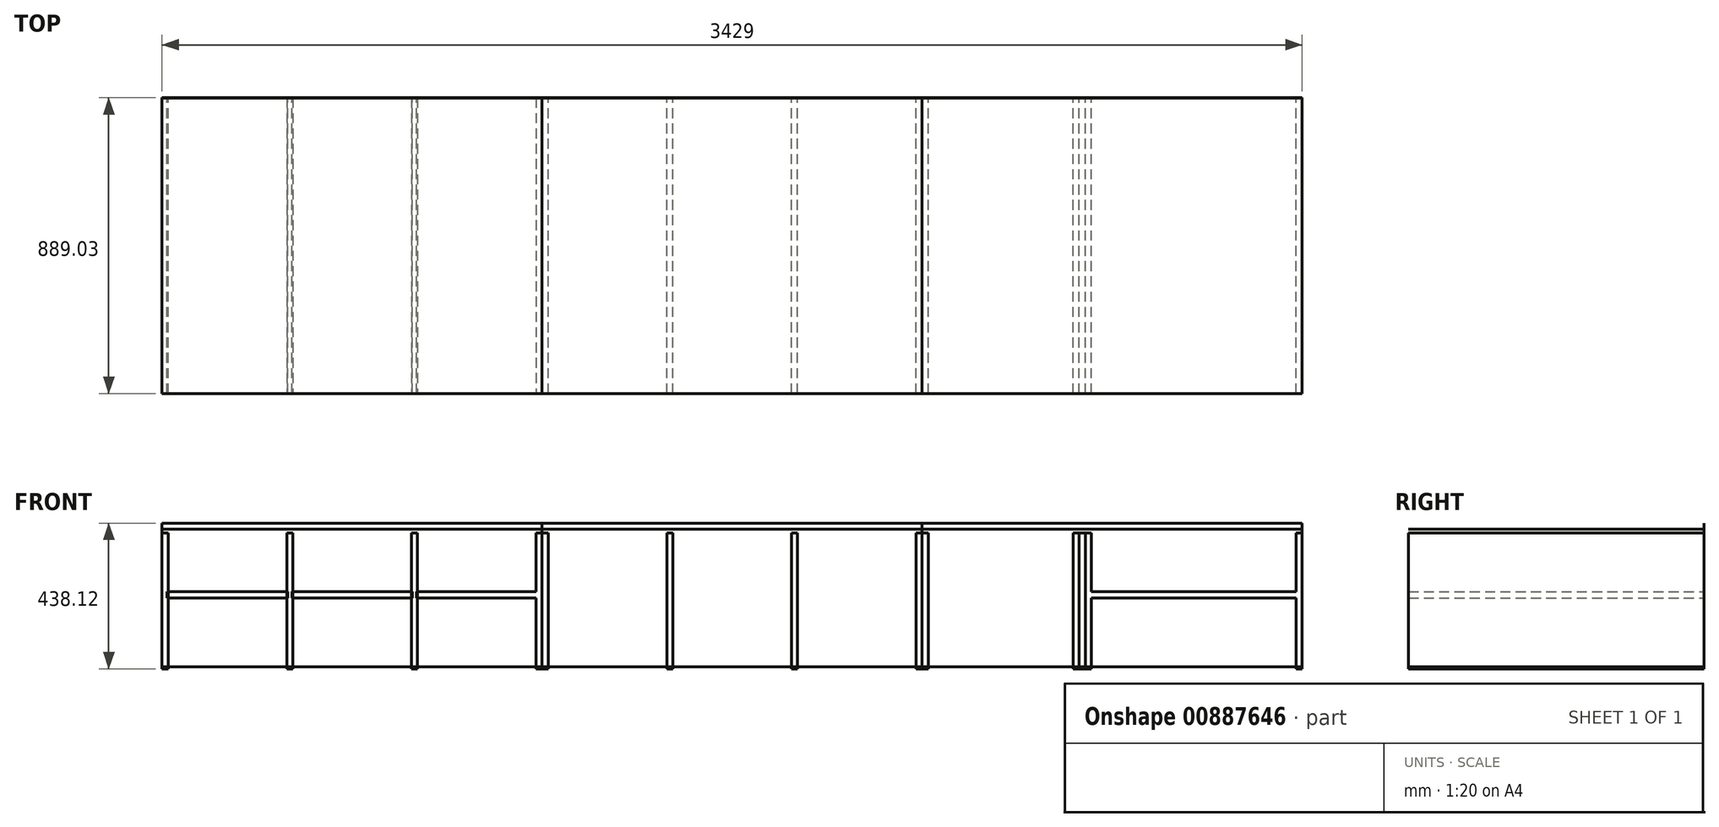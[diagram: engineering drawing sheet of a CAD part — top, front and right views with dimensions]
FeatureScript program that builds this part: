
annotation { "Feature Type Name" : "Feature", "Feature Type Description" : "" }
export const myFeature = defineFeature(function(context is Context, id is Id, definition is map)
    precondition{}
    {
        {
            var Q0;
            Q0=qCreatedBy(makeId("Front.planeOp"),FACE);
            var sketch = newSketch(context, id + "F0", { "sketchPlane" : qUnion([Q0])});
            skLineSegment(sketch, "E0.bottom", {"start": v(0, 0) * mm, "end": v(3429, 0) * mm, "construction": true});
            skLineSegment(sketch, "E0.top", {"start": v(0, 558.8) * mm, "end": v(3429, 558.8) * mm, "construction": true});
            skLineSegment(sketch, "E0.left", {"start": v(0, 0) * mm, "end": v(0, 558.8) * mm, "construction": true});
            skLineSegment(sketch, "E0.right", {"start": v(3429, 0) * mm, "end": v(3429, 558.8) * mm, "construction": true});
            skLineSegment(sketch, "E1", {"start": v(1714.5, 558.8) * mm, "end": v(1714.5, 0) * mm, "construction": true});
            skPoint(sketch, "E2", {"position": v(393.7, 558.8) * mm});
            skPoint(sketch, "E3", {"position": v(3035.3, 558.8) * mm});
            skSolve(sketch);
        }
        {
            var Q0;
            Q0=qCreatedBy(makeId("Top.planeOp"),FACE);
            var sketch = newSketch(context, id + "F1", { "sketchPlane" : qUnion([Q0])});
            skLineSegment(sketch, "E4.bottom", {"start": v(0, 0) * mm, "end": v(3429, 0) * mm, "construction": true});
            skLineSegment(sketch, "E4.top", {"start": v(0, -889) * mm, "end": v(3429, -889) * mm, "construction": true});
            skLineSegment(sketch, "E4.left", {"start": v(0, 0) * mm, "end": v(0, -889) * mm, "construction": true});
            skLineSegment(sketch, "E4.right", {"start": v(3429, 0) * mm, "end": v(3429, -889) * mm, "construction": true});
            skPoint(sketch, "E5.0", {"position": v(1714.5, 0) * mm});
            skLineSegment(sketch, "E6", {"start": v(1714.5, 0) * mm, "end": v(1714.5, -889) * mm, "construction": true});
            skPoint(sketch, "E7", {"position": v(3035.3, -889) * mm});
            skPoint(sketch, "E8", {"position": v(393.7, -889) * mm});
            skLineSegment(sketch, "E9", {"start": v(0, -444.5) * mm, "end": v(3429, -444.5) * mm, "construction": true});
            skPoint(sketch, "E10", {"position": v(0, -793.75) * mm});
            skPoint(sketch, "E11", {"position": v(0, -95.25) * mm});
            skPoint(sketch, "E12", {"position": v(3429, -95.25) * mm});
            skPoint(sketch, "E13", {"position": v(3429, -793.75) * mm});
            skPoint(sketch, "E14", {"position": v(1143, -889) * mm});
            skPoint(sketch, "E15", {"position": v(2286, -889) * mm});
            skSolve(sketch);
        }
        {
            var Q0;
            Q0=qCreatedBy(makeId("Top.planeOp"),FACE);
            var sketch = newSketch(context, id + "F2", { "sketchPlane" : qUnion([Q0])});
            skPoint(sketch, "E16.0", {"position": v(0, 0) * mm});
            skPoint(sketch, "E17.0", {"position": v(0, -889) * mm});
            skPoint(sketch, "E18.0", {"position": v(3429, -889) * mm});
            skPoint(sketch, "E19.0", {"position": v(3429, 0) * mm});
            skPoint(sketch, "E20.0", {"position": v(1143, -889) * mm});
            skPoint(sketch, "E21.0", {"position": v(2286, -889) * mm});
            skLineSegment(sketch, "E22.0", {"start": v(0, 0) * mm, "end": v(3429, 0) * mm, "construction": true});
            skLineSegment(sketch, "E23.bottom", {"start": v(0, 0) * mm, "end": v(1143, 0) * mm});
            skLineSegment(sketch, "E23.top", {"start": v(0, -889) * mm, "end": v(1143, -889) * mm});
            skLineSegment(sketch, "E23.left", {"start": v(0, 0) * mm, "end": v(0, -889) * mm});
            skLineSegment(sketch, "E23.right", {"start": v(1143, 0) * mm, "end": v(1143, -889) * mm});
            skLineSegment(sketch, "E24.bottom", {"start": v(1143, -889) * mm, "end": v(2286, -889) * mm});
            skLineSegment(sketch, "E24.top", {"start": v(1143, 0) * mm, "end": v(2286, 0) * mm});
            skLineSegment(sketch, "E24.left", {"start": v(1143, -889) * mm, "end": v(1143, 0) * mm});
            skLineSegment(sketch, "E24.right", {"start": v(2286, -889) * mm, "end": v(2286, 0) * mm});
            skLineSegment(sketch, "E25.bottom", {"start": v(2286, 0) * mm, "end": v(3429, 0) * mm});
            skLineSegment(sketch, "E25.top", {"start": v(2286, -889) * mm, "end": v(3429, -889) * mm});
            skLineSegment(sketch, "E25.left", {"start": v(2286, 0) * mm, "end": v(2286, -889) * mm});
            skLineSegment(sketch, "E25.right", {"start": v(3429, 0) * mm, "end": v(3429, -889) * mm});
            skSolve(sketch);
        }
        {
            var Q0;
            Q0=makeQuery(id+"F2.imprint","IMPRINT",FACE,{"disambiguationData":[TD([[makeQuery(id+"F2.imprint","IMPRINT",EDGE,{"derivedFrom":sQuery(id+"F2.wireOp",EDGE,"E23.bottom")}),-1.0]])]});
            extrude(context, id + "F3", {"entities" : qUnion([Q0]), "depth" : 23 / 812.8 * mm, "offsetDistance" : 25.4 * mm});
        }
        {
            var Q0;
            Q0=makeQuery(id+"F2.imprint","IMPRINT",FACE,{"disambiguationData":[TD([[makeQuery(id+"F2.imprint","IMPRINT",EDGE,{"derivedFrom":sQuery(id+"F2.wireOp",EDGE,"E24.bottom")}),1.0]])]});
            extrude(context, id + "F4", {"entities" : qUnion([Q0]), "depth" : 23 / 812.8 * mm, "offsetDistance" : 25.4 * mm});
        }
        {
            var Q0;
            Q0=makeQuery(id+"F2.imprint","IMPRINT",FACE,{"disambiguationData":[TD([[makeQuery(id+"F2.imprint","IMPRINT",EDGE,{"derivedFrom":sQuery(id+"F2.wireOp",EDGE,"E25.bottom")}),-1.0]])]});
            extrude(context, id + "F5", {"entities" : qUnion([Q0]), "depth" : 23 / 812.8 * mm, "offsetDistance" : 25.4 * mm});
        }
        {
            var Q0;
            Q0=makeQuery(id+"F3.opExtrude","CAP_FACE",FACE,{"disambiguationData":[OSD([sQuery(id+"F2.wireOp",EDGE,"E23.bottom"),sQuery(id+"F2.wireOp",EDGE,"E23.top"),sQuery(id+"F2.wireOp",EDGE,"E23.left"),sQuery(id+"F2.wireOp",EDGE,"E24.left")])],"isStart":false});
            var sketch = newSketch(context, id + "F6", { "sketchPlane" : qUnion([Q0])});
            skLineSegment(sketch, "E26.bottom", {"start": v(1143, -889) * mm, "end": v(1124.74, -889) * mm});
            skLineSegment(sketch, "E26.top", {"start": v(1143, 0) * mm, "end": v(1124.74, 0) * mm});
            skLineSegment(sketch, "E26.left", {"start": v(1143, -889) * mm, "end": v(1143, 0) * mm});
            skLineSegment(sketch, "E26.right", {"start": v(1124.74, -889) * mm, "end": v(1124.74, 0) * mm});
            skSolve(sketch);
        }
        {
            var Q0;
            Q0=makeQuery(id+"F6.imprint","IMPRINT",FACE,{"disambiguationData":[TD([[makeQuery(id+"F6.imprint","IMPRINT",EDGE,{"derivedFrom":sQuery(id+"F6.wireOp",EDGE,"E26.bottom")}),1.0]])]});
            extrude(context, id + "F7", {"entities" : qUnion([Q0]), "depth" : 401.64 * mm, "offsetDistance" : 25.4 * mm, "hasSecondDirection" : true, "secondDirectionOppositeDirection" : true, "secondDirectionDepth" : 6.35 * mm});
        }
        {
            var Q0;
            Q0=makeQuery(id+"F3.opExtrude","CAP_FACE",FACE,{"disambiguationData":[OSD([sQuery(id+"F2.wireOp",EDGE,"E23.bottom"),sQuery(id+"F2.wireOp",EDGE,"E23.top"),sQuery(id+"F2.wireOp",EDGE,"E23.left"),sQuery(id+"F2.wireOp",EDGE,"E24.left")])],"isStart":false});
            var sketch = newSketch(context, id + "F8", { "sketchPlane" : qUnion([Q0])});
            skLineSegment(sketch, "E27.bottom", {"start": v(0, -889) * mm, "end": v(18.26, -889) * mm});
            skLineSegment(sketch, "E27.top", {"start": v(0, 0) * mm, "end": v(18.26, 0) * mm});
            skLineSegment(sketch, "E27.left", {"start": v(0, -889) * mm, "end": v(0, 0) * mm});
            skLineSegment(sketch, "E27.right", {"start": v(18.26, -889) * mm, "end": v(18.26, 0) * mm});
            skSolve(sketch);
        }
        {
            var Q0;
            Q0 = qSketchRegion(id + "F8", true);
            extrude(context, id + "F9", {"entities" : qUnion([Q0]), "depth" : 401.64 * mm, "offsetDistance" : 25.4 * mm, "hasSecondDirection" : true, "secondDirectionOppositeDirection" : true, "secondDirectionDepth" : 6.35 * mm});
        }
        {
            var Q0;
            Q0=makeQuery(id+"F3.opExtrude","SWEPT_BODY",BODY,{"disambiguationData":[OSD([sQuery(id+"F2.wireOp",EDGE,"E23.bottom"),sQuery(id+"F2.wireOp",EDGE,"E23.top"),sQuery(id+"F2.wireOp",EDGE,"E23.left"),sQuery(id+"F2.wireOp",EDGE,"E24.left")])]});
            transform(context, id + "F10", {"entities" : qUnion([Q0]), "transformType" : TransformType.TRANSLATION_3D, "dx" : 0 * mm, "dy" : 0 * mm, "dz" : 413.54 * mm, "makeCopy" : true});
        }
        {
            var Q0;
            Q0=makeQuery(id+"F3.opExtrude","SWEPT_FACE",FACE,{"disambiguationData":[OSD([sQuery(id+"F2.wireOp",EDGE,"E23.bottom")])]});
            var sketch = newSketch(context, id + "F11", { "sketchPlane" : qUnion([Q0])});
            skPoint(sketch, "E28.0", {"position": v(-1133.87, 11.9) * mm});
            skLineSegment(sketch, "E29.0", {"start": v(-1124.74, 11.9) * mm, "end": v(-1143, 11.9) * mm, "construction": true});
            skLineSegment(sketch, "E30", {"start": v(-1133.87, 11.9) * mm, "end": v(-1133.87, 18.26) * mm, "construction": true});
            skLineSegment(sketch, "E31.0", {"start": v(0, 11.9) * mm, "end": v(-18.26, 11.9) * mm});
            skLineSegment(sketch, "E32", {"start": v(-9.13, 11.9) * mm, "end": v(-9.13, 18.26) * mm, "construction": true});
            skLineSegment(sketch, "E33", {"start": v(-1133.87, 18.26) * mm, "end": v(-758.96, 18.26) * mm, "construction": true});
            skLineSegment(sketch, "E34", {"start": v(-758.96, 18.26) * mm, "end": v(-384.04, 18.26) * mm, "construction": true});
            skLineSegment(sketch, "E35", {"start": v(-384.04, 18.26) * mm, "end": v(-9.13, 18.26) * mm, "construction": true});
            skSolve(sketch);
        }
        {
            var Q0;
            Q0=makeQuery(id+"F3.opExtrude","CAP_FACE",FACE,{"disambiguationData":[OSD([sQuery(id+"F2.wireOp",EDGE,"E23.bottom"),sQuery(id+"F2.wireOp",EDGE,"E23.top"),sQuery(id+"F2.wireOp",EDGE,"E23.left"),sQuery(id+"F2.wireOp",EDGE,"E24.left")])],"isStart":false});
            var sketch = newSketch(context, id + "F12", { "sketchPlane" : qUnion([Q0])});
            skPoint(sketch, "E36.0", {"position": v(758.96, 0) * mm});
            skPoint(sketch, "E36.1", {"position": v(384.04, 0) * mm});
            skLineSegment(sketch, "E37.bottom", {"start": v(749.83, 0) * mm, "end": v(768.09, 0) * mm});
            skLineSegment(sketch, "E37.top", {"start": v(749.83, -889) * mm, "end": v(768.09, -889) * mm});
            skLineSegment(sketch, "E37.left", {"start": v(749.83, 0) * mm, "end": v(749.83, -889) * mm});
            skLineSegment(sketch, "E37.right", {"start": v(768.09, 0) * mm, "end": v(768.09, -889) * mm});
            skLineSegment(sketch, "E38.bottom", {"start": v(374.91, 0) * mm, "end": v(393.17, 0) * mm});
            skLineSegment(sketch, "E38.top", {"start": v(374.91, -889) * mm, "end": v(393.17, -889) * mm});
            skLineSegment(sketch, "E38.left", {"start": v(374.91, 0) * mm, "end": v(374.91, -889) * mm});
            skLineSegment(sketch, "E38.right", {"start": v(393.17, 0) * mm, "end": v(393.17, -889) * mm});
            skSolve(sketch);
        }
        {
            var Q0;
            Q0=makeQuery(id+"F12.imprint","IMPRINT",FACE,{"disambiguationData":[TD([[makeQuery(id+"F12.imprint","IMPRINT",EDGE,{"derivedFrom":sQuery(id+"F12.wireOp",EDGE,"E37.bottom")}),-1.0]])]});
            var Q1;
            Q1=makeQuery(id+"F12.imprint","IMPRINT",FACE,{"disambiguationData":[TD([[makeQuery(id+"F12.imprint","IMPRINT",EDGE,{"derivedFrom":sQuery(id+"F12.wireOp",EDGE,"E38.bottom")}),-1.0]])]});
            extrude(context, id + "F13", {"entities" : qUnion([Q0, Q1]), "depth" : 401.64 * mm, "offsetDistance" : 25.4 * mm, "hasSecondDirection" : true, "secondDirectionOppositeDirection" : true, "secondDirectionDepth" : 6.35 * mm});
        }
        {
            var Q0;
            Q0=makeQuery(id+"F7.opExtrude","SWEPT_FACE",FACE,{"disambiguationData":[OSD([sQuery(id+"F6.wireOp",EDGE,"E26.top")])]});
            var sketch = newSketch(context, id + "F14", { "sketchPlane" : qUnion([Q0])});
            skPoint(sketch, "E39.0", {"position": v(-1124.74, 215.9) * mm});
            skPoint(sketch, "E39.1", {"position": v(-768.09, 215.9) * mm});
            skPoint(sketch, "E39.2", {"position": v(-749.83, 215.9) * mm});
            skPoint(sketch, "E39.3", {"position": v(-393.17, 215.9) * mm});
            skPoint(sketch, "E39.4", {"position": v(-374.91, 215.9) * mm});
            skPoint(sketch, "E39.5", {"position": v(-18.26, 215.9) * mm});
            skLineSegment(sketch, "E40", {"start": v(-1124.74, 215.9) * mm, "end": v(-1127.92, 215.9) * mm, "construction": true});
            skLineSegment(sketch, "E41", {"start": v(-768.09, 215.9) * mm, "end": v(-764.91, 215.9) * mm, "construction": true});
            skLineSegment(sketch, "E42", {"start": v(-749.83, 215.9) * mm, "end": v(-753, 215.9) * mm, "construction": true});
            skLineSegment(sketch, "E43.bottom", {"start": v(-1127.92, 225.03) * mm, "end": v(-764.91, 225.03) * mm});
            skLineSegment(sketch, "E43.top", {"start": v(-1127.92, 206.77) * mm, "end": v(-764.91, 206.77) * mm});
            skLineSegment(sketch, "E43.left", {"start": v(-1127.92, 225.03) * mm, "end": v(-1127.92, 206.77) * mm});
            skLineSegment(sketch, "E43.right", {"start": v(-764.91, 225.03) * mm, "end": v(-764.91, 206.77) * mm});
            skLineSegment(sketch, "E44.1.0.0", {"start": v(-753, 225.03) * mm, "end": v(-753, 206.77) * mm});
            skLineSegment(sketch, "E44.1.0.1", {"start": v(-753, 225.03) * mm, "end": v(-390, 225.03) * mm});
            skLineSegment(sketch, "E44.1.0.2", {"start": v(-753, 206.77) * mm, "end": v(-390, 206.77) * mm});
            skLineSegment(sketch, "E44.1.0.3", {"start": v(-390, 225.03) * mm, "end": v(-390, 206.77) * mm});
            skLineSegment(sketch, "E44.2.0.0", {"start": v(-378.09, 225.03) * mm, "end": v(-378.09, 206.77) * mm});
            skLineSegment(sketch, "E44.2.0.1", {"start": v(-378.09, 225.03) * mm, "end": v(-15.08, 225.03) * mm});
            skLineSegment(sketch, "E44.2.0.2", {"start": v(-378.09, 206.77) * mm, "end": v(-15.08, 206.77) * mm});
            skLineSegment(sketch, "E44.2.0.3", {"start": v(-15.08, 225.03) * mm, "end": v(-15.08, 206.77) * mm});
            skLineSegment(sketch, "E44.direction1", {"start": v(-753, 206.77) * mm, "end": v(-1127.92, 206.77) * mm, "construction": true});
            skSolve(sketch);
        }
        {
            var Q0;
            Q0=makeQuery(id+"F14.imprint","IMPRINT",FACE,{"disambiguationData":[TD([[makeQuery(id+"F14.imprint","IMPRINT",EDGE,{"derivedFrom":sQuery(id+"F14.wireOp",EDGE,"E44.2.0.0")}),1.0]])]});
            var Q1;
            Q1=makeQuery(id+"F14.imprint","IMPRINT",FACE,{"disambiguationData":[TD([[makeQuery(id+"F14.imprint","IMPRINT",EDGE,{"derivedFrom":sQuery(id+"F14.wireOp",EDGE,"E44.1.0.0")}),1.0]])]});
            var Q2;
            {var subQ0=sQuery(id+"F14.wireOp",EDGE,"E43.right");Q2=makeQuery(id+"F14.imprint","IMPRINT",FACE,{"disambiguationData":[TD([[makeQuery(id+"F14.imprint","IMPRINT",EDGE,{"derivedFrom":subQ0}),-1.0]])]});}
            var Q3;
            Q3=makeQuery(id+"F13.opExtrude","SWEPT_FACE",FACE,{"disambiguationData":[OSD([sQuery(id+"F12.wireOp",EDGE,"E37.top")])]});
            extrude(context, id + "F15", {"entities" : qUnion([Q0, Q1, Q2]), "endBound" : BoundingType.UP_TO_SURFACE, "oppositeDirection" : true, "depth" : 25.4 * mm, "endBoundEntityFace" : qUnion([Q3]), "offsetDistance" : 25.4 * mm});
        }
        {
            var Q0;
            Q0=makeQuery(id+"F15.opExtrude","SWEPT_FACE",FACE,{"disambiguationData":[OSD([sQuery(id+"F2.wireOp",EDGE,"E23.bottom"),sQuery(id+"F6.wireOp",EDGE,"E26.top"),sQuery(id+"F6.wireOp",EDGE,"E26.right")])]});
            extrude(context, id + "F16", {"entities" : qUnion([Q0]), "operationType" : NewBodyOperationType.ADD, "depth" : 3.17 * mm, "offsetDistance" : 25.4 * mm});
        }
        {
            var Q0;
            Q0=makeQuery(id+"F4.opExtrude","CAP_FACE",FACE,{"disambiguationData":[OSD([sQuery(id+"F2.wireOp",EDGE,"E24.bottom"),sQuery(id+"F2.wireOp",EDGE,"E24.top"),sQuery(id+"F2.wireOp",EDGE,"E24.left"),sQuery(id+"F2.wireOp",EDGE,"E25.left")])],"isStart":false});
            var sketch = newSketch(context, id + "F17", { "sketchPlane" : qUnion([Q0])});
            skLineSegment(sketch, "E45.bottom", {"start": v(1143, -889) * mm, "end": v(1161.26, -889) * mm});
            skLineSegment(sketch, "E45.top", {"start": v(1143, 0) * mm, "end": v(1161.26, 0) * mm});
            skLineSegment(sketch, "E45.left", {"start": v(1143, -889) * mm, "end": v(1143, 0) * mm});
            skLineSegment(sketch, "E45.right", {"start": v(1161.26, -889) * mm, "end": v(1161.26, 0) * mm});
            skSolve(sketch);
        }
        {
            var Q0;
            Q0=makeQuery(id+"F17.imprint","IMPRINT",FACE,{"disambiguationData":[TD([[makeQuery(id+"F17.imprint","IMPRINT",EDGE,{"derivedFrom":sQuery(id+"F17.wireOp",EDGE,"E45.bottom")}),1.0]])]});
            extrude(context, id + "F18", {"entities" : qUnion([Q0]), "depth" : 401.64 * mm, "offsetDistance" : 25.4 * mm, "hasSecondDirection" : true, "secondDirectionOppositeDirection" : true, "secondDirectionDepth" : 6.35 * mm});
        }
        {
            var Q0;
            Q0=makeQuery(id+"F4.opExtrude","CAP_FACE",FACE,{"disambiguationData":[OSD([sQuery(id+"F2.wireOp",EDGE,"E24.bottom"),sQuery(id+"F2.wireOp",EDGE,"E24.top"),sQuery(id+"F2.wireOp",EDGE,"E24.left"),sQuery(id+"F2.wireOp",EDGE,"E25.left")])],"isStart":false});
            var sketch = newSketch(context, id + "F19", { "sketchPlane" : qUnion([Q0])});
            skLineSegment(sketch, "E46.bottom", {"start": v(2286, -889) * mm, "end": v(2267.74, -889) * mm});
            skLineSegment(sketch, "E46.top", {"start": v(2286, 0) * mm, "end": v(2267.74, 0) * mm});
            skLineSegment(sketch, "E46.left", {"start": v(2286, -889) * mm, "end": v(2286, 0) * mm});
            skLineSegment(sketch, "E46.right", {"start": v(2267.74, -889) * mm, "end": v(2267.74, 0) * mm});
            skSolve(sketch);
        }
        {
            var Q0;
            Q0=makeQuery(id+"F19.imprint","IMPRINT",FACE,{"disambiguationData":[TD([[makeQuery(id+"F19.imprint","IMPRINT",EDGE,{"derivedFrom":sQuery(id+"F19.wireOp",EDGE,"E46.bottom")}),1.0]])]});
            extrude(context, id + "F20", {"entities" : qUnion([Q0]), "depth" : 401.64 * mm, "offsetDistance" : 25.4 * mm, "hasSecondDirection" : true, "secondDirectionOppositeDirection" : true, "secondDirectionDepth" : 6.35 * mm});
        }
        {
            var Q0;
            Q0=makeQuery(id+"F4.opExtrude","SWEPT_BODY",BODY,{"disambiguationData":[OSD([sQuery(id+"F2.wireOp",EDGE,"E24.bottom"),sQuery(id+"F2.wireOp",EDGE,"E24.top"),sQuery(id+"F2.wireOp",EDGE,"E24.left"),sQuery(id+"F2.wireOp",EDGE,"E25.left")])]});
            transform(context, id + "F21", {"entities" : qUnion([Q0]), "transformType" : TransformType.TRANSLATION_3D, "dx" : 0 * mm, "dy" : 0 * mm, "dz" : 413.54 * mm, "makeCopy" : true});
        }
        {
            var Q0;
            Q0=makeQuery(id+"F4.opExtrude","SWEPT_FACE",FACE,{"disambiguationData":[OSD([sQuery(id+"F2.wireOp",EDGE,"E24.bottom")])]});
            var sketch = newSketch(context, id + "F22", { "sketchPlane" : qUnion([Q0])});
            skPoint(sketch, "E47.0", {"position": v(1152.13, 11.9) * mm});
            skLineSegment(sketch, "E48", {"start": v(1152.13, 11.9) * mm, "end": v(1152.13, 18.26) * mm, "construction": true});
            skPoint(sketch, "E49.0", {"position": v(2276.87, 11.9) * mm});
            skLineSegment(sketch, "E50", {"start": v(2276.87, 11.9) * mm, "end": v(2276.87, 18.26) * mm, "construction": true});
            skLineSegment(sketch, "E51", {"start": v(1152.13, 18.26) * mm, "end": v(1527.04, 18.26) * mm, "construction": true});
            skLineSegment(sketch, "E52", {"start": v(1527.04, 18.26) * mm, "end": v(1901.96, 18.26) * mm, "construction": true});
            skLineSegment(sketch, "E53", {"start": v(1901.96, 18.26) * mm, "end": v(2276.87, 18.26) * mm, "construction": true});
            skSolve(sketch);
        }
        {
            var Q0;
            Q0=makeQuery(id+"F4.opExtrude","CAP_FACE",FACE,{"disambiguationData":[OSD([sQuery(id+"F2.wireOp",EDGE,"E24.bottom"),sQuery(id+"F2.wireOp",EDGE,"E24.top"),sQuery(id+"F2.wireOp",EDGE,"E24.left"),sQuery(id+"F2.wireOp",EDGE,"E25.left")])],"isStart":false});
            var sketch = newSketch(context, id + "F23", { "sketchPlane" : qUnion([Q0])});
            skPoint(sketch, "E54.0", {"position": v(1527.04, -889) * mm});
            skPoint(sketch, "E54.1", {"position": v(1901.96, -889) * mm});
            skLineSegment(sketch, "E55.bottom", {"start": v(1536.17, -889) * mm, "end": v(1517.91, -889) * mm});
            skLineSegment(sketch, "E55.top", {"start": v(1536.17, 0) * mm, "end": v(1517.91, 0) * mm});
            skLineSegment(sketch, "E55.left", {"start": v(1536.17, -889) * mm, "end": v(1536.17, 0) * mm});
            skLineSegment(sketch, "E55.right", {"start": v(1517.91, -889) * mm, "end": v(1517.91, 0) * mm});
            skLineSegment(sketch, "E56.bottom", {"start": v(1911.09, -889) * mm, "end": v(1892.83, -889) * mm});
            skLineSegment(sketch, "E56.top", {"start": v(1911.09, 0) * mm, "end": v(1892.83, 0) * mm});
            skLineSegment(sketch, "E56.left", {"start": v(1911.09, -889) * mm, "end": v(1911.09, 0) * mm});
            skLineSegment(sketch, "E56.right", {"start": v(1892.83, -889) * mm, "end": v(1892.83, 0) * mm});
            skSolve(sketch);
        }
        {
            var Q0;
            Q0=makeQuery(id+"F23.imprint","IMPRINT",FACE,{"disambiguationData":[TD([[makeQuery(id+"F23.imprint","IMPRINT",EDGE,{"derivedFrom":sQuery(id+"F23.wireOp",EDGE,"E55.bottom")}),1.0]])]});
            var Q1;
            Q1=makeQuery(id+"F23.imprint","IMPRINT",FACE,{"disambiguationData":[TD([[makeQuery(id+"F23.imprint","IMPRINT",EDGE,{"derivedFrom":sQuery(id+"F23.wireOp",EDGE,"E56.bottom")}),1.0]])]});
            var Q2;
            Q2=makeQuery(id+"F18.opExtrude","CAP_VERTEX",VERTEX,{"disambiguationData":[OSD([sQuery(id+"F2.wireOp",EDGE,"E24.bottom"),sQuery(id+"F17.wireOp",EDGE,"E45.bottom"),sQuery(id+"F17.wireOp",EDGE,"E45.right")])],"isStart":false});
            var Q3;
            Q3=makeQuery(id+"F18.opExtrude","CAP_VERTEX",VERTEX,{"disambiguationData":[OSD([sQuery(id+"F2.wireOp",EDGE,"E24.bottom"),sQuery(id+"F17.wireOp",EDGE,"E45.bottom"),sQuery(id+"F17.wireOp",EDGE,"E45.right")])],"isStart":true});
            extrude(context, id + "F24", {"entities" : qUnion([Q0, Q1]), "endBound" : BoundingType.UP_TO_VERTEX, "depth" : 25.4 * mm, "endBoundEntityVertex" : qUnion([Q2]), "offsetDistance" : 25.4 * mm, "hasSecondDirection" : true, "secondDirectionBound" : SecondDirectionBoundingType.UP_TO_VERTEX, "secondDirectionOppositeDirection" : true, "secondDirectionDepth" : 25.4 * mm, "secondDirectionBoundEntityVertex" : qUnion([Q3])});
        }
        {
            var Q0;
            Q0=makeQuery(id+"F5.opExtrude","CAP_FACE",FACE,{"disambiguationData":[OSD([sQuery(id+"F2.wireOp",EDGE,"E25.bottom"),sQuery(id+"F2.wireOp",EDGE,"E25.top"),sQuery(id+"F2.wireOp",EDGE,"E25.left"),sQuery(id+"F2.wireOp",EDGE,"E25.right")])],"isStart":false});
            var sketch = newSketch(context, id + "F25", { "sketchPlane" : qUnion([Q0])});
            skLineSegment(sketch, "E57.bottom", {"start": v(2286, -889) * mm, "end": v(2304.26, -889) * mm});
            skLineSegment(sketch, "E57.top", {"start": v(2286, 0) * mm, "end": v(2304.26, 0) * mm});
            skLineSegment(sketch, "E57.left", {"start": v(2286, -889) * mm, "end": v(2286, 0) * mm});
            skLineSegment(sketch, "E57.right", {"start": v(2304.26, -889) * mm, "end": v(2304.26, 0) * mm});
            skLineSegment(sketch, "E58.bottom", {"start": v(3429, -889) * mm, "end": v(3410.74, -889) * mm});
            skLineSegment(sketch, "E58.top", {"start": v(3429, 0) * mm, "end": v(3410.74, 0) * mm});
            skLineSegment(sketch, "E58.left", {"start": v(3429, -889) * mm, "end": v(3429, 0) * mm});
            skLineSegment(sketch, "E58.right", {"start": v(3410.74, -889) * mm, "end": v(3410.74, 0) * mm});
            skSolve(sketch);
        }
        {
            var Q0;
            Q0=makeQuery(id+"F25.imprint","IMPRINT",FACE,{"disambiguationData":[TD([[makeQuery(id+"F25.imprint","IMPRINT",EDGE,{"derivedFrom":sQuery(id+"F25.wireOp",EDGE,"E57.bottom")}),1.0]])]});
            extrude(context, id + "F26", {"entities" : qUnion([Q0]), "depth" : 401.64 * mm, "offsetDistance" : 25.4 * mm, "hasSecondDirection" : true, "secondDirectionOppositeDirection" : true, "secondDirectionDepth" : 6.35 * mm});
        }
        {
            var Q0;
            Q0 = qSketchRegion(id + "F25", true);
            var Q1;
            Q1=makeQuery(id+"F26.opExtrude","CAP_VERTEX",VERTEX,{"disambiguationData":[OSD([sQuery(id+"F2.wireOp",EDGE,"E25.top"),sQuery(id+"F25.wireOp",EDGE,"E57.bottom"),sQuery(id+"F25.wireOp",EDGE,"E57.right")])],"isStart":false});
            var Q2;
            Q2=makeQuery(id+"F26.opExtrude","CAP_VERTEX",VERTEX,{"disambiguationData":[OSD([sQuery(id+"F2.wireOp",EDGE,"E25.top"),sQuery(id+"F25.wireOp",EDGE,"E57.bottom"),sQuery(id+"F25.wireOp",EDGE,"E57.right")])],"isStart":true});
            extrude(context, id + "F27", {"entities" : qUnion([Q0]), "endBound" : BoundingType.UP_TO_VERTEX, "depth" : 25.4 * mm, "endBoundEntityVertex" : qUnion([Q1]), "offsetDistance" : 25.4 * mm, "hasSecondDirection" : true, "secondDirectionBound" : SecondDirectionBoundingType.UP_TO_VERTEX, "secondDirectionOppositeDirection" : true, "secondDirectionDepth" : 25.4 * mm, "secondDirectionBoundEntityVertex" : qUnion([Q2])});
        }
        {
            var Q0;
            Q0=makeQuery(id+"F5.opExtrude","SWEPT_BODY",BODY,{"disambiguationData":[OSD([sQuery(id+"F2.wireOp",EDGE,"E25.bottom"),sQuery(id+"F2.wireOp",EDGE,"E25.top"),sQuery(id+"F2.wireOp",EDGE,"E25.left"),sQuery(id+"F2.wireOp",EDGE,"E25.right")])]});
            transform(context, id + "F28", {"entities" : qUnion([Q0]), "transformType" : TransformType.TRANSLATION_3D, "dx" : 0 * mm, "dy" : 0 * mm, "dz" : 413.54 * mm, "makeCopy" : true});
        }
        {
            var Q0;
            Q0=makeQuery(id+"F5.opExtrude","CAP_FACE",FACE,{"disambiguationData":[OSD([sQuery(id+"F2.wireOp",EDGE,"E25.bottom"),sQuery(id+"F2.wireOp",EDGE,"E25.top"),sQuery(id+"F2.wireOp",EDGE,"E25.left"),sQuery(id+"F2.wireOp",EDGE,"E25.right")])],"isStart":false});
            var sketch = newSketch(context, id + "F29", { "sketchPlane" : qUnion([Q0])});
            skLineSegment(sketch, "E59", {"start": v(3410.74, 0) * mm, "end": v(3410.74, -889) * mm});
            skLineSegment(sketch, "E60", {"start": v(2304.26, 0) * mm, "end": v(2304.26, -889) * mm});
            skLineSegment(sketch, "E61.bottom", {"start": v(2794.8, -889) * mm, "end": v(2776.54, -889) * mm});
            skLineSegment(sketch, "E61.top", {"start": v(2794.8, 0) * mm, "end": v(2776.54, 0) * mm});
            skLineSegment(sketch, "E61.left", {"start": v(2794.8, -889) * mm, "end": v(2794.8, 0) * mm});
            skLineSegment(sketch, "E61.right", {"start": v(2776.54, -889) * mm, "end": v(2776.54, 0) * mm});
            skLineSegment(sketch, "E62.bottom", {"start": v(2776.54, -889) * mm, "end": v(2758.28, -889) * mm});
            skLineSegment(sketch, "E62.top", {"start": v(2776.54, 0) * mm, "end": v(2758.28, 0) * mm});
            skLineSegment(sketch, "E62.right", {"start": v(2758.28, -889) * mm, "end": v(2758.28, 0) * mm});
            skLineSegment(sketch, "E63.bottom", {"start": v(2758.28, -889) * mm, "end": v(2740.03, -889) * mm});
            skLineSegment(sketch, "E63.top", {"start": v(2758.28, 0) * mm, "end": v(2740.03, 0) * mm});
            skLineSegment(sketch, "E63.right", {"start": v(2740.03, -889) * mm, "end": v(2740.03, 0) * mm});
            skSolve(sketch);
        }
        {
            var Q0;
            Q0=makeQuery(id+"F29.imprint","IMPRINT",FACE,{"disambiguationData":[TD([[makeQuery(id+"F29.imprint","IMPRINT",EDGE,{"derivedFrom":sQuery(id+"F29.wireOp",EDGE,"E61.bottom")}),1.0]])]});
            var Q1;
            Q1=makeQuery(id+"F27.opExtrude","CAP_VERTEX",VERTEX,{"disambiguationData":[OSD([sQuery(id+"F25.wireOp",EDGE,"E58.bottom"),sQuery(id+"F25.wireOp",EDGE,"E58.right")])],"isStart":false});
            var Q2;
            Q2=makeQuery(id+"F27.opExtrude","CAP_VERTEX",VERTEX,{"disambiguationData":[OSD([sQuery(id+"F25.wireOp",EDGE,"E58.bottom"),sQuery(id+"F25.wireOp",EDGE,"E58.right")])],"isStart":true});
            extrude(context, id + "F30", {"entities" : qUnion([Q0]), "endBound" : BoundingType.UP_TO_VERTEX, "depth" : 25.4 * mm, "endBoundEntityVertex" : qUnion([Q1]), "offsetDistance" : 25.4 * mm, "hasSecondDirection" : true, "secondDirectionBound" : SecondDirectionBoundingType.UP_TO_VERTEX, "secondDirectionOppositeDirection" : true, "secondDirectionDepth" : 25.4 * mm, "secondDirectionBoundEntityVertex" : qUnion([Q2])});
        }
        {
            var Q0;
            Q0=makeQuery(id+"F29.imprint","IMPRINT",FACE,{"disambiguationData":[TD([[makeQuery(id+"F29.imprint","IMPRINT",EDGE,{"derivedFrom":sQuery(id+"F29.wireOp",EDGE,"E62.bottom")}),1.0]])]});
            var Q1;
            Q1=makeQuery(id+"F30.opExtrude","CAP_VERTEX",VERTEX,{"disambiguationData":[OSD([sQuery(id+"F29.wireOp",EDGE,"E61.bottom"),sQuery(id+"F29.wireOp",EDGE,"E61.right")])],"isStart":false});
            var Q2;
            Q2=makeQuery(id+"F30.opExtrude","CAP_VERTEX",VERTEX,{"disambiguationData":[OSD([sQuery(id+"F29.wireOp",EDGE,"E61.bottom"),sQuery(id+"F29.wireOp",EDGE,"E61.right")])],"isStart":true});
            extrude(context, id + "F31", {"entities" : qUnion([Q0]), "endBound" : BoundingType.UP_TO_VERTEX, "depth" : 25.4 * mm, "endBoundEntityVertex" : qUnion([Q1]), "offsetDistance" : 25.4 * mm, "hasSecondDirection" : true, "secondDirectionBound" : SecondDirectionBoundingType.UP_TO_VERTEX, "secondDirectionOppositeDirection" : true, "secondDirectionDepth" : 25.4 * mm, "secondDirectionBoundEntityVertex" : qUnion([Q2])});
        }
        {
            var Q0;
            Q0=makeQuery(id+"F29.imprint","IMPRINT",FACE,{"disambiguationData":[TD([[makeQuery(id+"F29.imprint","IMPRINT",EDGE,{"derivedFrom":sQuery(id+"F29.wireOp",EDGE,"E63.bottom")}),1.0]])]});
            var Q1;
            Q1=makeQuery(id+"F31.opExtrude","CAP_VERTEX",VERTEX,{"disambiguationData":[OSD([sQuery(id+"F29.wireOp",EDGE,"E62.bottom"),sQuery(id+"F29.wireOp",EDGE,"E62.right")])],"isStart":false});
            var Q2;
            Q2=makeQuery(id+"F31.opExtrude","CAP_VERTEX",VERTEX,{"disambiguationData":[OSD([sQuery(id+"F29.wireOp",EDGE,"E62.bottom"),sQuery(id+"F29.wireOp",EDGE,"E62.right")])],"isStart":true});
            extrude(context, id + "F32", {"entities" : qUnion([Q0]), "endBound" : BoundingType.UP_TO_VERTEX, "depth" : 25.4 * mm, "endBoundEntityVertex" : qUnion([Q1]), "offsetDistance" : 25.4 * mm, "hasSecondDirection" : true, "secondDirectionBound" : SecondDirectionBoundingType.UP_TO_VERTEX, "secondDirectionOppositeDirection" : true, "secondDirectionDepth" : 25.4 * mm, "secondDirectionBoundEntityVertex" : qUnion([Q2])});
        }
        {
            var Q0;
            Q0=makeQuery(id+"F30.opExtrude","SWEPT_FACE",FACE,{"disambiguationData":[OSD([sQuery(id+"F29.wireOp",EDGE,"E61.left")])]});
            var sketch = newSketch(context, id + "F33", { "sketchPlane" : qUnion([Q0])});
            skLineSegment(sketch, "E64.bottom", {"start": v(-889, 225.03) * mm, "end": v(0, 225.03) * mm});
            skLineSegment(sketch, "E64.top", {"start": v(-889, 206.77) * mm, "end": v(0, 206.77) * mm});
            skLineSegment(sketch, "E64.left", {"start": v(-889, 225.03) * mm, "end": v(-889, 206.77) * mm});
            skLineSegment(sketch, "E64.right", {"start": v(0, 225.03) * mm, "end": v(0, 206.77) * mm});
            skSolve(sketch);
        }
        {
            var Q0;
            Q0=makeQuery(id+"F33.imprint","IMPRINT",FACE,{"disambiguationData":[TD([[makeQuery(id+"F33.imprint","IMPRINT",EDGE,{"derivedFrom":sQuery(id+"F33.wireOp",EDGE,"E64.bottom")}),-1.0]])]});
            extrude(context, id + "F34", {"entities" : qUnion([Q0]), "endBound" : BoundingType.UP_TO_NEXT, "depth" : 25.4 * mm, "offsetDistance" : 25.4 * mm});
        }
        {
            var Q0;
            Q0=makeQuery(id+"F33.imprint","IMPRINT",FACE,{"disambiguationData":[TD([[makeQuery(id+"F33.imprint","IMPRINT",EDGE,{"derivedFrom":sQuery(id+"F33.wireOp",EDGE,"E64.bottom")}),-1.0]])]});
            extrude(context, id + "F35", {"entities" : qUnion([Q0]), "operationType" : NewBodyOperationType.ADD, "oppositeDirection" : true, "depth" : 6.35 * mm, "offsetDistance" : 25.4 * mm});
        }
        {
            var Q0;
            Q0=makeQuery(id+"F34.opExtrude","CAP_FACE",FACE,{"disambiguationData":[OSD([sQuery(id+"F33.wireOp",EDGE,"E64.bottom"),sQuery(id+"F33.wireOp",EDGE,"E64.top"),sQuery(id+"F33.wireOp",EDGE,"E64.left"),sQuery(id+"F33.wireOp",EDGE,"E64.right")])],"isStart":false});
            extrude(context, id + "F36", {"entities" : qUnion([Q0]), "operationType" : NewBodyOperationType.ADD, "depth" : 3.17 * mm, "offsetDistance" : 25.4 * mm});
        }
        {
            var Q0;
            Q0=makeQuery(id+"F28.opPattern","COPY",FACE,{"derivedFrom":makeQuery(id+"F5.opExtrude","SWEPT_FACE",FACE,{"disambiguationData":[OSD([sQuery(id+"F2.wireOp",EDGE,"E25.bottom")])]}),"instanceName":"1"});
            var sketch = newSketch(context, id + "F37", { "sketchPlane" : qUnion([Q0])});
            skPoint(sketch, "E65.0", {"position": v(-3429, 431.8) * mm});
            skPoint(sketch, "E66.0", {"position": v(-2286, 0) * mm});
            skPoint(sketch, "E67.0", {"position": v(-1143, 431.8) * mm});
            skPoint(sketch, "E68.0", {"position": v(0, 0) * mm});
            skLineSegment(sketch, "E69.bottom", {"start": v(0, 0) * mm, "end": v(-1143, 0) * mm});
            skLineSegment(sketch, "E69.top", {"start": v(0, 431.8) * mm, "end": v(-1143, 431.8) * mm});
            skLineSegment(sketch, "E69.left", {"start": v(0, 0) * mm, "end": v(0, 431.8) * mm});
            skLineSegment(sketch, "E69.right", {"start": v(-1143, 0) * mm, "end": v(-1143, 431.8) * mm});
            skLineSegment(sketch, "E70.bottom", {"start": v(-1143, 431.8) * mm, "end": v(-2286, 431.8) * mm});
            skLineSegment(sketch, "E70.top", {"start": v(-1143, 0) * mm, "end": v(-2286, 0) * mm});
            skLineSegment(sketch, "E70.left", {"start": v(-1143, 431.8) * mm, "end": v(-1143, 0) * mm});
            skLineSegment(sketch, "E70.right", {"start": v(-2286, 431.8) * mm, "end": v(-2286, 0) * mm});
            skLineSegment(sketch, "E71.bottom", {"start": v(-2286, 0) * mm, "end": v(-3429, 0) * mm});
            skLineSegment(sketch, "E71.top", {"start": v(-2286, 431.8) * mm, "end": v(-3429, 431.8) * mm});
            skLineSegment(sketch, "E71.left", {"start": v(-2286, 0) * mm, "end": v(-2286, 431.8) * mm});
            skLineSegment(sketch, "E71.right", {"start": v(-3429, 0) * mm, "end": v(-3429, 431.8) * mm});
            skSolve(sketch);
        }
        {
            var Q0;
            {var subQ0=sQuery(id+"F37.wireOp",EDGE,"E71.top");Q0=makeQuery(id+"F37.imprint","IMPRINT",FACE,{"disambiguationData":[TD([[makeQuery(id+"F37.imprint","IMPRINT",EDGE,{"derivedFrom":subQ0}),1.0]])]});}
            var Q1;
            {var subQ0=sQuery(id+"F37.wireOp",EDGE,"E71.bottom");Q1=makeQuery(id+"F37.imprint","IMPRINT",FACE,{"disambiguationData":[TD([[makeQuery(id+"F37.imprint","IMPRINT",EDGE,{"derivedFrom":subQ0}),-1.0]])]});}
            extrude(context, id + "F38", {"entities" : qUnion([Q0, Q1]), "depth" : 23 / 812.8 * mm, "offsetDistance" : 25.4 * mm});
        }
        {
            var Q0;
            {var subQ3=sQuery(id+"F37.wireOp",EDGE,"E70.bottom");Q0=makeQuery(id+"F37.imprint","IMPRINT",FACE,{"disambiguationData":[TD([[makeQuery(id+"F37.imprint","IMPRINT",EDGE,{"derivedFrom":subQ3}),1.0]])]});}
            extrude(context, id + "F39", {"entities" : qUnion([Q0]), "depth" : 23 / 812.8 * mm, "offsetDistance" : 25.4 * mm});
        }
        {
            var Q0;
            Q0=makeQuery(id+"F37.imprint","IMPRINT",FACE,{"disambiguationData":[TD([[makeQuery(id+"F37.imprint","IMPRINT",EDGE,{"derivedFrom":sQuery(id+"F37.wireOp",EDGE,"E69.bottom")}),-1.0]])]});
            extrude(context, id + "F40", {"entities" : qUnion([Q0]), "depth" : 23 / 812.8 * mm, "offsetDistance" : 25.4 * mm});
        }
    });
